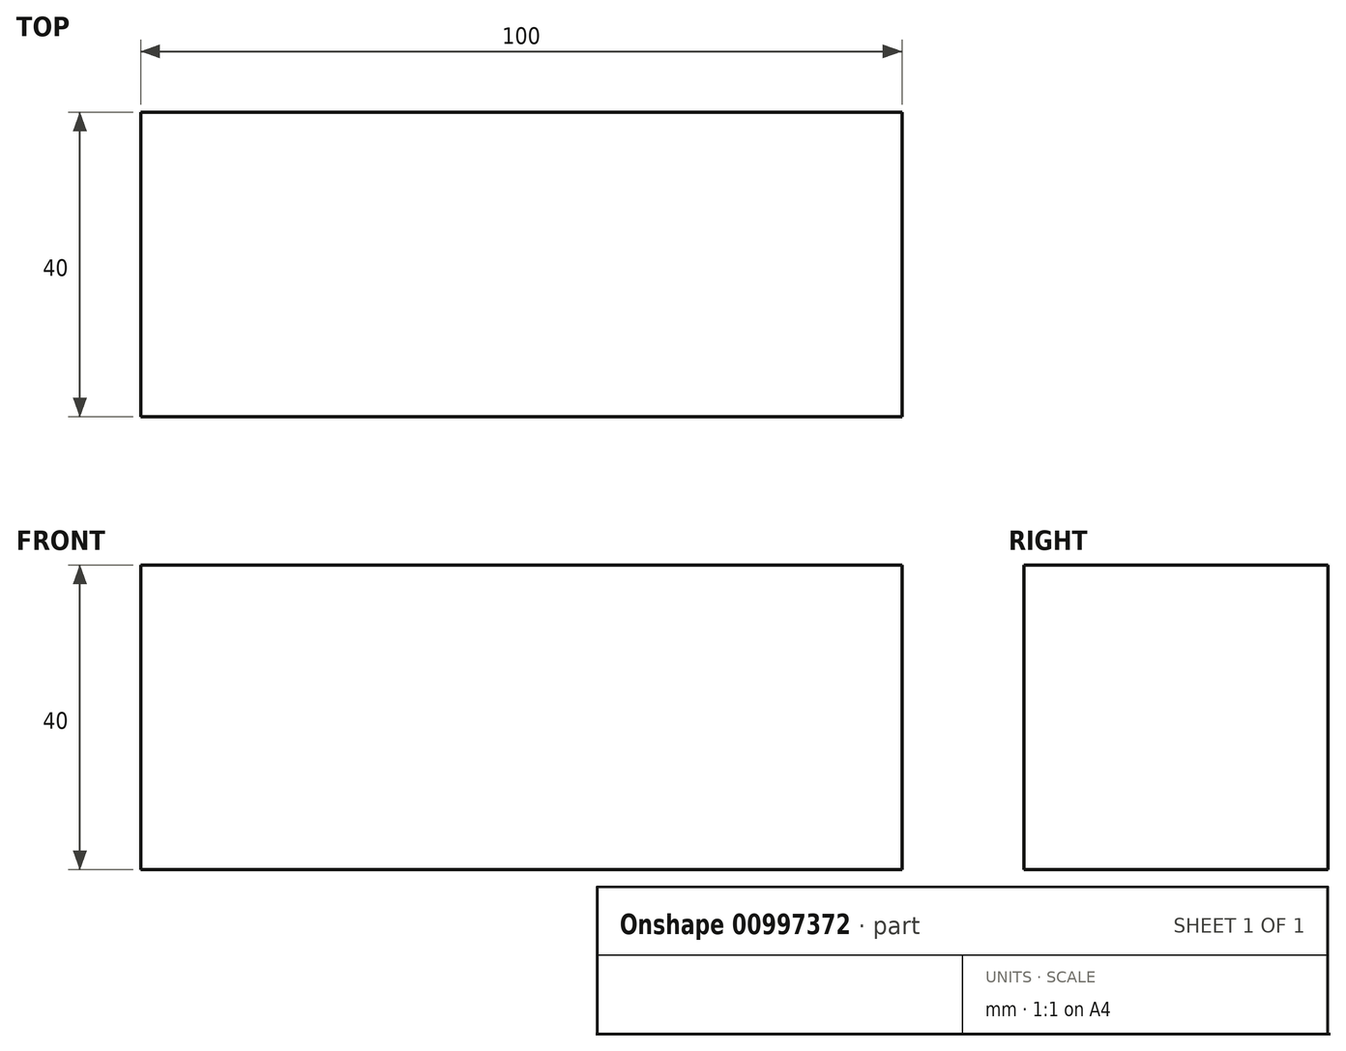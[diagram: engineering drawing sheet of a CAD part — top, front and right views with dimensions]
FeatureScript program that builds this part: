
annotation { "Feature Type Name" : "Feature", "Feature Type Description" : "" }
export const myFeature = defineFeature(function(context is Context, id is Id, definition is map)
    precondition{}
    {
        {
            var Q0;
            Q0=qCreatedBy(makeId("Front.planeOp"),FACE);
            var sketch = newSketch(context, id + "F0", { "sketchPlane" : qUnion([Q0])});
            skLineSegment(sketch, "E0.bottom", {"start": v(0, 0) * mm, "end": v(100, 0) * mm});
            skLineSegment(sketch, "E0.top", {"start": v(0, -40) * mm, "end": v(100, -40) * mm});
            skLineSegment(sketch, "E0.left", {"start": v(0, 0) * mm, "end": v(0, -40) * mm});
            skLineSegment(sketch, "E0.right", {"start": v(100, 0) * mm, "end": v(100, -40) * mm});
            skSolve(sketch);
        }
        {
            var Q0;
            Q0 = qSketchRegion(id + "F0", true);
            extrude(context, id + "F1", {"entities" : qUnion([Q0]), "depth" : 40 * mm, "offsetDistance" : 25 * mm});
        }
    });
